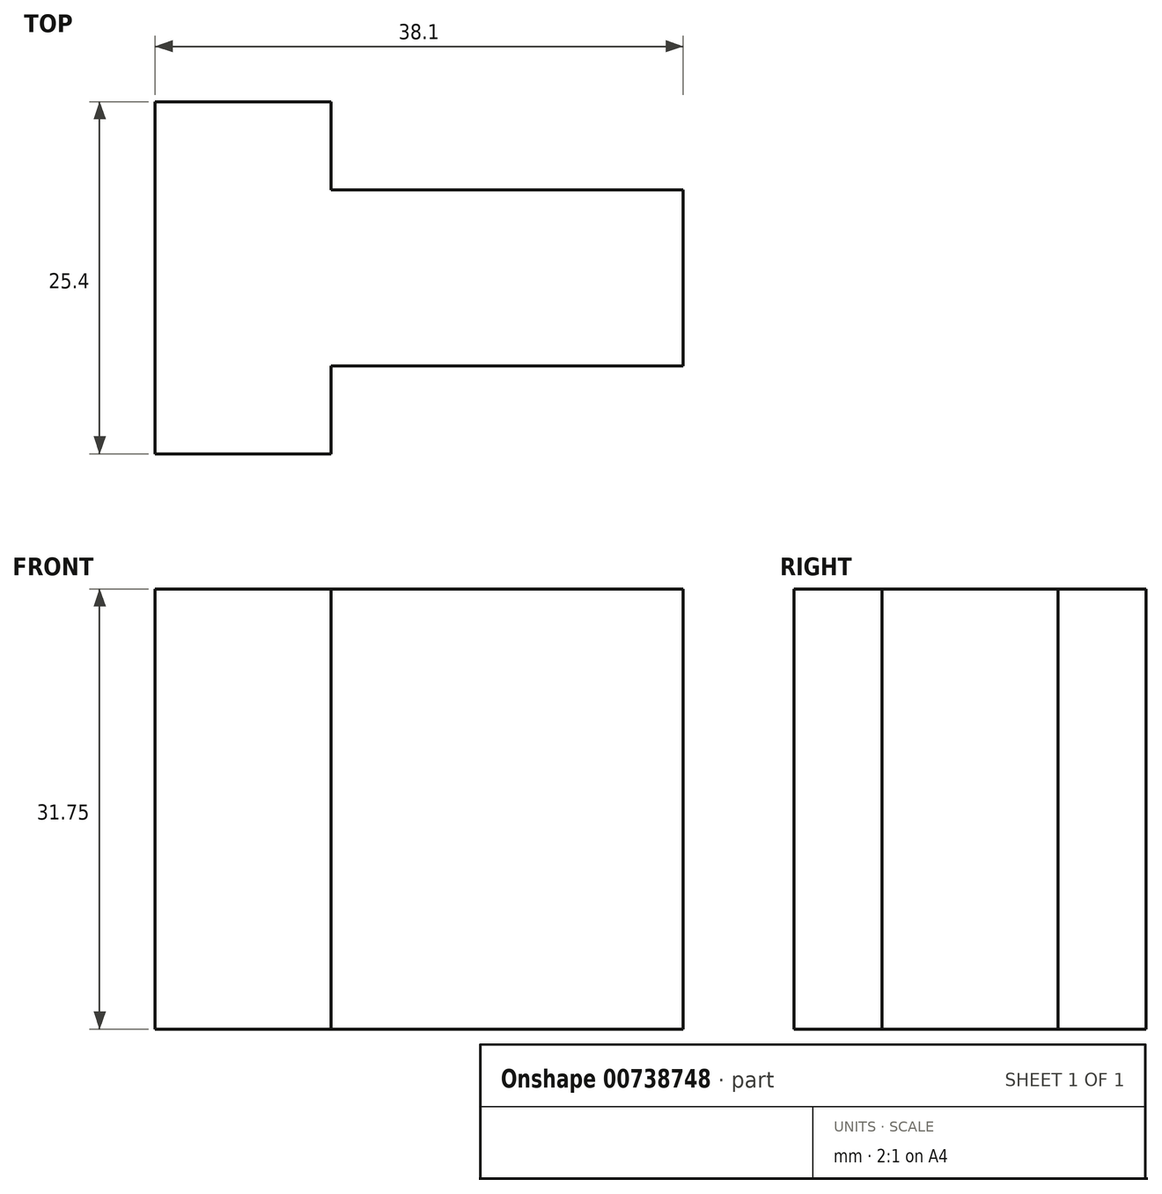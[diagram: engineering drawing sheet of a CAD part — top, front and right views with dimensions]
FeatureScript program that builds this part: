
annotation { "Feature Type Name" : "Feature", "Feature Type Description" : "" }
export const myFeature = defineFeature(function(context is Context, id is Id, definition is map)
    precondition{}
    {
        {
            var Q0;
            Q0=qCreatedBy(makeId("Front.planeOp"),FACE);
            var sketch = newSketch(context, id + "F0", { "sketchPlane" : qUnion([Q0])});
            skLineSegment(sketch, "E0", {"start": v(0, 0) * mm, "end": v(0, 31.75) * mm});
            skLineSegment(sketch, "E1", {"start": v(0, 31.75) * mm, "end": v(38.1, 31.75) * mm});
            skLineSegment(sketch, "E2", {"start": v(38.1, 31.75) * mm, "end": v(38.1, 0) * mm});
            skLineSegment(sketch, "E3", {"start": v(0, 0) * mm, "end": v(38.1, 0) * mm});
            skSolve(sketch);
        }
        {
            var Q0;
            Q0 = qSketchRegion(id + "F0", true);
            extrude(context, id + "F1", {"entities" : qUnion([Q0]), "depth" : 25.4 * mm, "offsetDistance" : 25.4 * mm});
        }
        {
            var Q0;
            Q0=makeQuery(id+"F1.opExtrude","SWEPT_FACE",FACE,{"disambiguationData":[OSD([sQuery(id+"F0.wireOp",EDGE,"E1")])]});
            var sketch = newSketch(context, id + "F2", { "sketchPlane" : qUnion([Q0])});
            skLineSegment(sketch, "E4", {"start": v(12.7, -25.4) * mm, "end": v(12.7, -19.05) * mm});
            skLineSegment(sketch, "E5", {"start": v(12.7, -19.05) * mm, "end": v(38.1, -19.05) * mm});
            skLineSegment(sketch, "E6", {"start": v(38.1, -19.05) * mm, "end": v(38.1, -25.4) * mm});
            skLineSegment(sketch, "E7", {"start": v(38.1, -25.4) * mm, "end": v(12.7, -25.4) * mm});
            skLineSegment(sketch, "E8", {"start": v(12.7, 0) * mm, "end": v(12.7, -6.35) * mm});
            skLineSegment(sketch, "E9", {"start": v(12.7, -6.35) * mm, "end": v(38.1, -6.35) * mm});
            skLineSegment(sketch, "E10", {"start": v(38.1, -6.35) * mm, "end": v(38.1, 0) * mm});
            skLineSegment(sketch, "E11", {"start": v(38.1, 0) * mm, "end": v(12.7, 0) * mm});
            skSolve(sketch);
        }
        {
            var Q0;
            Q0=makeQuery(id+"F2.imprint","IMPRINT",FACE,{"disambiguationData":[TD([[makeQuery(id+"F2.imprint","IMPRINT",EDGE,{"derivedFrom":sQuery(id+"F2.wireOp",EDGE,"E8")}),1.0]])]});
            extrude(context, id + "F3", {"entities" : qUnion([Q0]), "operationType" : NewBodyOperationType.REMOVE, "endBound" : BoundingType.THROUGH_ALL, "oppositeDirection" : true, "depth" : 25.4 * mm, "offsetDistance" : 25.4 * mm});
        }
        {
            var Q0;
            Q0=makeQuery(id+"F1.opExtrude","SWEPT_FACE",FACE,{"disambiguationData":[OSD([sQuery(id+"F0.wireOp",EDGE,"E1")])]});
            var sketch = newSketch(context, id + "F4", { "sketchPlane" : qUnion([Q0])});
            skLineSegment(sketch, "E12", {"start": v(12.7, -25.4) * mm, "end": v(12.7, -19.05) * mm});
            skLineSegment(sketch, "E13", {"start": v(12.7, -19.05) * mm, "end": v(38.1, -19.05) * mm});
            skLineSegment(sketch, "E14", {"start": v(38.1, -19.05) * mm, "end": v(38.1, -25.4) * mm});
            skLineSegment(sketch, "E15", {"start": v(38.1, -25.4) * mm, "end": v(12.7, -25.4) * mm});
            skSolve(sketch);
        }
        {
            var Q0;
            Q0=makeQuery(id+"F4.imprint","IMPRINT",FACE,{"disambiguationData":[TD([[makeQuery(id+"F4.imprint","IMPRINT",EDGE,{"derivedFrom":sQuery(id+"F4.wireOp",EDGE,"E12")}),-1.0]])]});
            extrude(context, id + "F5", {"entities" : qUnion([Q0]), "operationType" : NewBodyOperationType.REMOVE, "endBound" : BoundingType.THROUGH_ALL, "oppositeDirection" : true, "depth" : 25.4 * mm, "offsetDistance" : 25.4 * mm});
        }
    });
